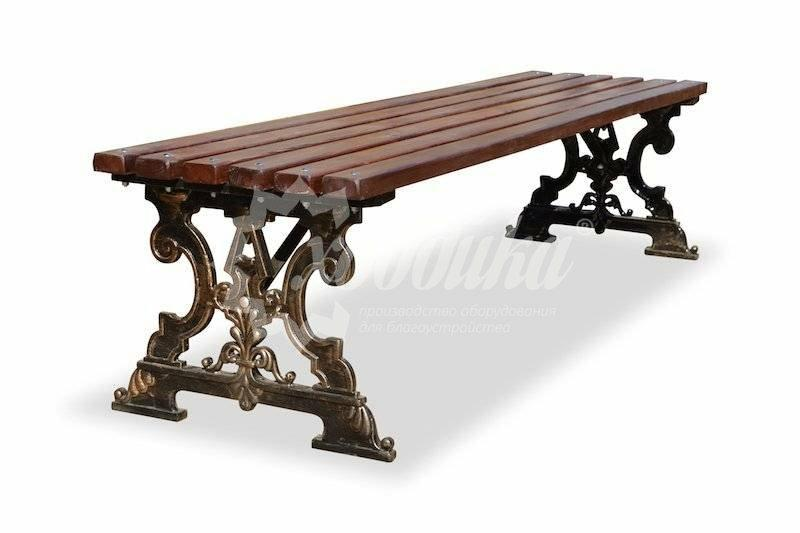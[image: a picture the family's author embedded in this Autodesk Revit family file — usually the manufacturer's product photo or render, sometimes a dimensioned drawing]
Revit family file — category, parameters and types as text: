
# Revit family: 9535 Банкетка чугунная «Ампир» Хоббика
name_source: partatom
category: Антураж
revit_build: Autodesk Revit 2018 (Build: 20180423_1000(x64)
units: mm (PartAtom-declared; Revit-internal decimal feet)

## family parameters
Всегда вертикально = Да
Источник визуального образа = Геометрия семейства
На основе рабочей плоскости = Нет
Общий = Нет
При загрузке вырезать с полостями = Нет
Точка расчета площади = Нет

## types (4) — shared parameters
URL = https://hobbyka.ru
Артикул товара = Арт. 9535
Высота = 390 мм
Группа модели = Садовые скамейки
Изготовитель = ООО «Хоббика»
Изображение типоразмера = Банкетка чугунная «Ампир» Арт 9535.jpg
Материал изделия = Чугун, дерево
Цвет опоры = Чугун
Цвет сидения = Дерево
Ширина = 480 мм

## per-type parameters (varying)
| type | Версия 1,5 м | Версия 1,8 м | Версия 2,0 м | Версия 3,0 м | Длина | Описание | Средняя опора |
| Версия 1,5 м | Да | Нет | Нет | Нет | 1500 мм | Банкетка чугунная «Ампир». Венрси 1,5 м | Нет |
| Версия 1,8 м | Нет | Да | Нет | Нет | 1800 мм | Банкетка чугунная «Ампир». Венрси 1,8 м | Нет |
| Версия 2,0 м | Нет | Нет | Да | Нет | 2000 мм | Банкетка чугунная «Ампир». Венрси 2,0 м | Да |
| Версия 3,0 м | Нет | Нет | Нет | Да | 3000 мм | Банкетка чугунная «Ампир». Венрси 3,0 м | Да |
